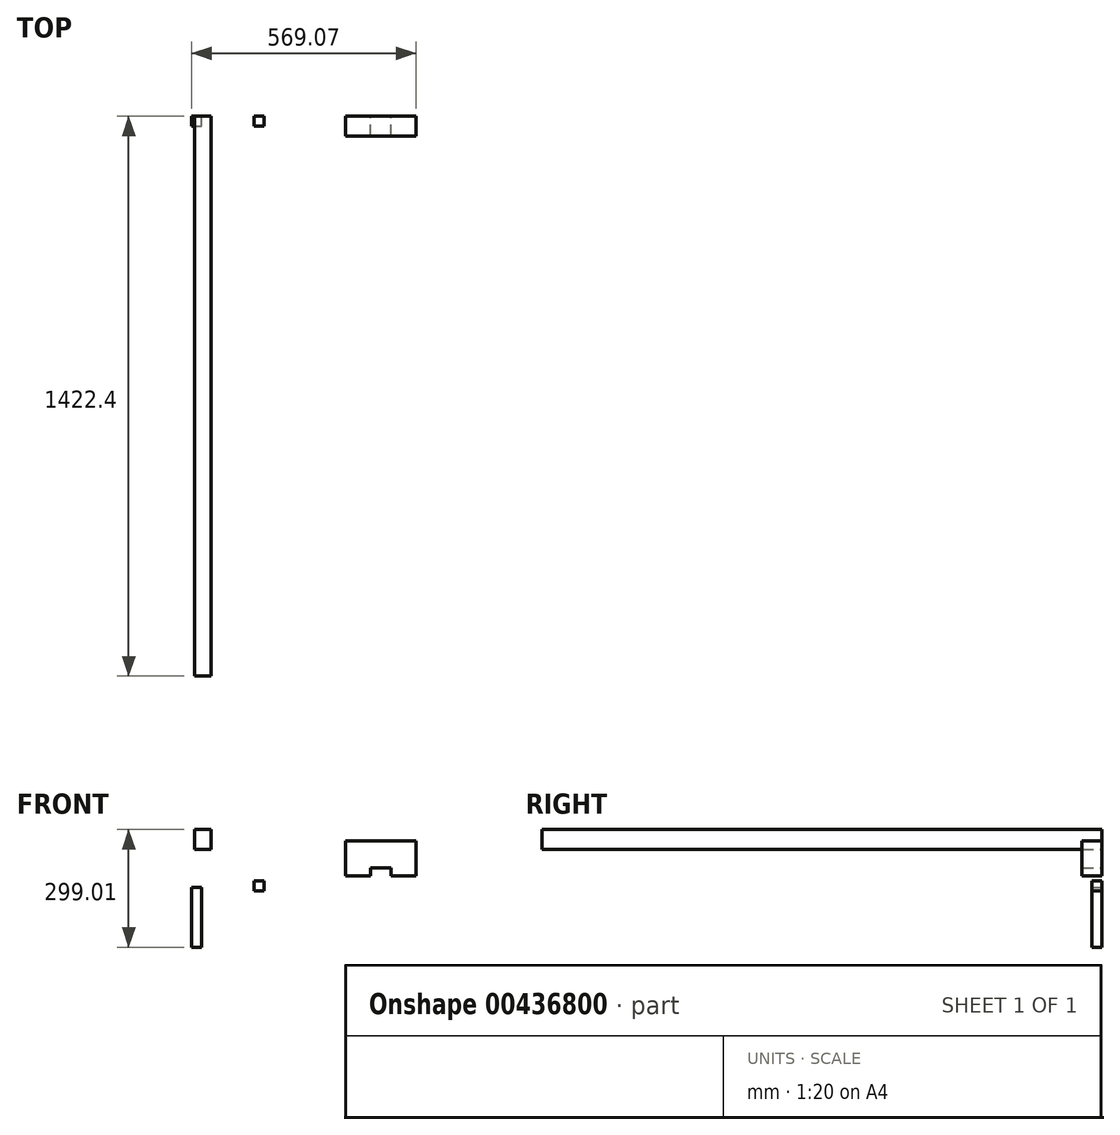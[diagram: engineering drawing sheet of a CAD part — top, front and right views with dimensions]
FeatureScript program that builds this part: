
annotation { "Feature Type Name" : "Feature", "Feature Type Description" : "" }
export const myFeature = defineFeature(function(context is Context, id is Id, definition is map)
    precondition{}
    {
        {
            var Q0;
            Q0=qCreatedBy(makeId("Front.planeOp"),FACE);
            var sketch = newSketch(context, id + "F0", { "sketchPlane" : qUnion([Q0])});
            skLineSegment(sketch, "E0.bottom", {"start": v(-89.89, 51.04) * mm, "end": v(-47.89, 51.04) * mm});
            skLineSegment(sketch, "E0.top", {"start": v(-89.89, 0.24) * mm, "end": v(-47.89, 0.24) * mm});
            skLineSegment(sketch, "E0.left", {"start": v(-89.89, 51.04) * mm, "end": v(-89.89, 0.24) * mm});
            skLineSegment(sketch, "E0.right", {"start": v(-47.89, 51.04) * mm, "end": v(-47.89, 0.24) * mm});
            skLineSegment(sketch, "E1.bottom", {"start": v(61.1, -79.33) * mm, "end": v(86.5, -79.33) * mm});
            skLineSegment(sketch, "E1.top", {"start": v(61.1, -104.73) * mm, "end": v(86.5, -104.73) * mm});
            skLineSegment(sketch, "E1.left", {"start": v(61.1, -79.33) * mm, "end": v(61.1, -104.73) * mm});
            skLineSegment(sketch, "E1.right", {"start": v(86.5, -79.33) * mm, "end": v(86.5, -104.73) * mm});
            skLineSegment(sketch, "E2.bottom", {"start": v(-96.94, -95.57) * mm, "end": v(-71.54, -95.57) * mm});
            skLineSegment(sketch, "E2.top", {"start": v(-96.94, -247.97) * mm, "end": v(-71.54, -247.97) * mm});
            skLineSegment(sketch, "E2.left", {"start": v(-96.94, -95.57) * mm, "end": v(-96.94, -247.97) * mm});
            skLineSegment(sketch, "E2.right", {"start": v(-71.54, -95.57) * mm, "end": v(-71.54, -247.97) * mm});
            skLineSegment(sketch, "E3.bottom", {"start": v(294.33, 21.7) * mm, "end": v(472.13, 21.7) * mm});
            skLineSegment(sketch, "E3.top", {"start": v(294.33, -67.2) * mm, "end": v(472.13, -67.2) * mm});
            skLineSegment(sketch, "E3.left", {"start": v(294.33, 21.7) * mm, "end": v(294.33, -67.2) * mm});
            skLineSegment(sketch, "E3.right", {"start": v(472.13, 21.7) * mm, "end": v(472.13, -67.2) * mm});
            skLineSegment(sketch, "E4", {"start": v(383.23, 21.7) * mm, "end": v(383.23, -67.2) * mm, "construction": true});
            skLineSegment(sketch, "E5.bottom", {"start": v(357.83, -67.2) * mm, "end": v(408.63, -67.2) * mm});
            skLineSegment(sketch, "E5.top", {"start": v(357.83, -46.2) * mm, "end": v(408.63, -46.2) * mm});
            skLineSegment(sketch, "E5.left", {"start": v(357.83, -67.2) * mm, "end": v(357.83, -46.2) * mm});
            skLineSegment(sketch, "E5.right", {"start": v(408.63, -67.2) * mm, "end": v(408.63, -46.2) * mm});
            skSolve(sketch);
        }
        {
            var Q0;
            Q0=makeQuery(id+"F0.imprint","IMPRINT",FACE,{"disambiguationData":[TD([[makeQuery(id+"F0.imprint","IMPRINT",EDGE,{"derivedFrom":sQuery(id+"F0.wireOp",EDGE,"EYHh0keZ-dq85-RoP4-cdDx-edc1yLFaoymn.bottom")}),-1.0]])]});
            var Q1;
            Q1=makeQuery(id+"F0.imprint","IMPRINT",FACE,{"disambiguationData":[TD([[makeQuery(id+"F0.imprint","IMPRINT",EDGE,{"derivedFrom":sQuery(id+"F0.wireOp",EDGE,"UadvPcKm-j0qG-JEAH-zla8-nYVUKiOehe4D.bottom")}),-1.0]])]});
            var Q2;
            Q2=makeQuery(id+"F0.imprint","IMPRINT",FACE,{"disambiguationData":[TD([[makeQuery(id+"F0.imprint","IMPRINT",EDGE,{"derivedFrom":sQuery(id+"F0.wireOp",EDGE,"2oHyTkdA-lQSc-7H5n-ySbw-x8OOMB2U3htZ.bottom")}),1.0]])]});
            var Q3;
            Q3=makeQuery(id+"F0.imprint","IMPRINT",FACE,{"disambiguationData":[TD([[makeQuery(id+"F0.imprint","IMPRINT",EDGE,{"derivedFrom":sQuery(id+"F0.wireOp",EDGE,"cdPn9m90-VgNk-awHr-Mxcp-u1gyEFDMjo4V.bottom")}),-1.0]])]});
            var Q4;
            Q4=makeQuery(id+"F0.imprint","IMPRINT",FACE,{"disambiguationData":[TD([[makeQuery(id+"F0.imprint","IMPRINT",EDGE,{"derivedFrom":sQuery(id+"F0.wireOp",EDGE,"E3.bottom")}),-1.0]])]});
            var Q5;
            Q5=makeQuery(id+"F0.imprint","IMPRINT",FACE,{"disambiguationData":[TD([[makeQuery(id+"F0.imprint","IMPRINT",EDGE,{"derivedFrom":sQuery(id+"F0.wireOp",EDGE,"3nWd816j-FVwJ-FnN5-mij7-t4TUHYOI2Q3C.bottom")}),-1.0]])]});
            extrude(context, id + "F1", {"entities" : qUnion([Q0, Q1, Q2, Q3, Q4, Q5]), "depth" : 50.8 * mm});
        }
        {
            var Q0;
            Q0=makeQuery(id+"F0.imprint","IMPRINT",FACE,{"disambiguationData":[TD([[makeQuery(id+"F0.imprint","IMPRINT",EDGE,{"derivedFrom":sQuery(id+"F0.wireOp",EDGE,"E0.bottom")}),-1.0]])]});
            extrude(context, id + "F2", {"entities" : qUnion([Q0]), "depth" : 1422.4 * mm});
        }
        {
            var Q0;
            Q0=makeQuery(id+"F0.imprint","IMPRINT",FACE,{"disambiguationData":[TD([[makeQuery(id+"F0.imprint","IMPRINT",EDGE,{"derivedFrom":sQuery(id+"F0.wireOp",EDGE,"E1.bottom")}),-1.0]])]});
            var Q1;
            Q1=makeQuery(id+"F0.imprint","IMPRINT",FACE,{"disambiguationData":[TD([[makeQuery(id+"F0.imprint","IMPRINT",EDGE,{"derivedFrom":sQuery(id+"F0.wireOp",EDGE,"E2.bottom")}),-1.0]])]});
            extrude(context, id + "F3", {"entities" : qUnion([Q0, Q1]), "depth" : 25.4 * mm});
        }
    });
